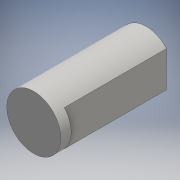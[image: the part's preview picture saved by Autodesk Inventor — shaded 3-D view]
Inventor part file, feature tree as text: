
AUTODESK INVENTOR PART (.ipt)
format: ipt  version: 2016 (Build 200138000, 138)  size: 95,744 bytes
history: native  units: mm
features: extrude x2, sketch x2, other x1
ambient origin geometry x8: Origin, YZ Plane, XZ Plane, XY Plane, X Axis, Y Axis, Z Axis, Center Point
bodies: Body1 (feature_tree)
feature tree (5):
  other  "ソリッド1"
  extrude  "押し出し1"  Depth=12.0mm
  extrude  "押し出し3"  Depth=25.0mm TaperAngle=0.0deg
  sketch  "スケッチ1"
  sketch  "スケッチ4"
